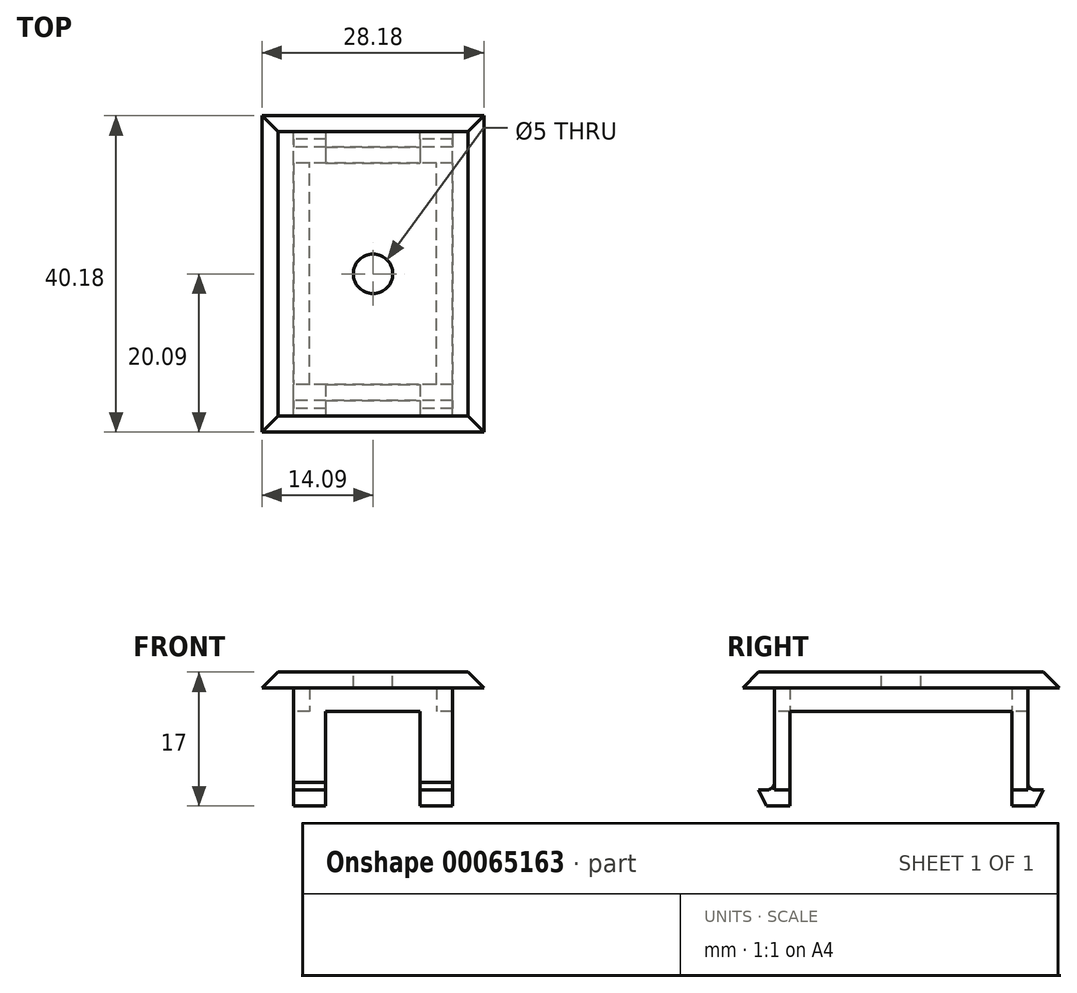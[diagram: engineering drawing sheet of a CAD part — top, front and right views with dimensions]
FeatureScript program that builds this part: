
annotation { "Feature Type Name" : "Feature", "Feature Type Description" : "" }
export const myFeature = defineFeature(function(context is Context, id is Id, definition is map)
    precondition{}
    {
        {
            var Q0;
            Q0=qCreatedBy(makeId("Top.planeOp"),FACE);
            var sketch = newSketch(context, id + "F0", { "sketchPlane" : qUnion([Q0])});
            skLineSegment(sketch, "E0.rect.bottom", {"start": v(10.1, -16.09) * mm, "end": v(-10.1, -16.09) * mm});
            skLineSegment(sketch, "E0.rect.top", {"start": v(10.1, 16.09) * mm, "end": v(-10.1, 16.09) * mm});
            skLineSegment(sketch, "E0.rect.left", {"start": v(10.1, -16.09) * mm, "end": v(10.1, 16.09) * mm});
            skLineSegment(sketch, "E0.rect.right", {"start": v(-10.1, -16.09) * mm, "end": v(-10.09, 16.09) * mm});
            skPoint(sketch, "E0.rect.middle", {"position": v(0, 0) * mm});
            skLineSegment(sketch, "E1.rect.bottom", {"start": v(8.1, 14.1) * mm, "end": v(-8.09, 14.1) * mm});
            skLineSegment(sketch, "E1.rect.top", {"start": v(8.09, -14.1) * mm, "end": v(-8.1, -14.1) * mm});
            skLineSegment(sketch, "E1.rect.left", {"start": v(8.1, 14.09) * mm, "end": v(8.1, -14.1) * mm});
            skLineSegment(sketch, "E1.rect.right", {"start": v(-8.1, 14.1) * mm, "end": v(-8.1, -14.09) * mm});
            skSolve(sketch);
        }
        {
            var Q0;
            Q0=makeQuery(id+"F0.imprint","IMPRINT",FACE,{"disambiguationData":[TD([[makeQuery(id+"F0.imprint","IMPRINT",EDGE,{"derivedFrom":sQuery(id+"F0.wireOp",EDGE,"E0.rect.bottom")}),-1.0]])]});
            extrude(context, id + "F1", {"entities" : qUnion([Q0]), "depth" : 13 * mm});
        }
        {
            var Q0;
            Q0=makeQuery(id+"F1.opExtrude","CAP_FACE",FACE,{"disambiguationData":[OSD([sQuery(id+"F0.wireOp",EDGE,"E0.rect.bottom"),sQuery(id+"F0.wireOp",EDGE,"E0.rect.top"),sQuery(id+"F0.wireOp",EDGE,"E0.rect.left"),sQuery(id+"F0.wireOp",EDGE,"E0.rect.right"),sQuery(id+"F0.wireOp",EDGE,"E1.rect.bottom"),sQuery(id+"F0.wireOp",EDGE,"E1.rect.top"),sQuery(id+"F0.wireOp",EDGE,"E1.rect.left"),sQuery(id+"F0.wireOp",EDGE,"E1.rect.right")])],"isStart":false});
            var sketch = newSketch(context, id + "F2", { "sketchPlane" : qUnion([Q0])});
            skLineSegment(sketch, "E2.rect.bottom", {"start": v(14.1, 20.09) * mm, "end": v(-14.09, 20.09) * mm});
            skLineSegment(sketch, "E2.rect.top", {"start": v(14.1, -20.09) * mm, "end": v(-14.09, -20.09) * mm});
            skLineSegment(sketch, "E2.rect.left", {"start": v(14.1, 20.09) * mm, "end": v(14.1, -20.09) * mm});
            skLineSegment(sketch, "E2.rect.right", {"start": v(-14.09, 20.09) * mm, "end": v(-14.09, -20.09) * mm});
            skPoint(sketch, "E2.rect.middle", {"position": v(0, 0) * mm});
            skSolve(sketch);
        }
        {
            var Q0;
            Q0=makeQuery(id+"F2.imprint","IMPRINT",FACE,{"disambiguationData":[TD([[makeQuery(id+"F2.imprint","IMPRINT",EDGE,{"derivedFrom":makeQuery(id+"F1.opExtrude","CAP_EDGE",EDGE,{"disambiguationData":[OSD([sQuery(id+"F0.wireOp",EDGE,"E1.rect.bottom")])],"isStart":false})}),1.0]])]});
            var Q1;
            Q1=makeQuery(id+"F2.imprint","IMPRINT",FACE,{"disambiguationData":[TD([[makeQuery(id+"F2.imprint","IMPRINT",EDGE,{"derivedFrom":makeQuery(id+"F1.opExtrude","CAP_EDGE",EDGE,{"disambiguationData":[OSD([sQuery(id+"F0.wireOp",EDGE,"E0.rect.bottom")])],"isStart":false})}),-1.0]])]});
            var Q2;
            Q2=makeQuery(id+"F2.imprint","IMPRINT",FACE,{"disambiguationData":[TD([[makeQuery(id+"F2.imprint","IMPRINT",EDGE,{"derivedFrom":sQuery(id+"F2.wireOp",EDGE,"E2.rect.bottom")}),1.0]])]});
            extrude(context, id + "F3", {"entities" : qUnion([Q0, Q1, Q2]), "operationType" : NewBodyOperationType.ADD, "depth" : 2 * mm});
        }
        {
            var Q0;
            Q0=makeQuery(id+"F3.opExtrude","CAP_EDGE",EDGE,{"disambiguationData":[OSD([sQuery(id+"F2.wireOp",EDGE,"E2.rect.top")])],"isStart":false});
            var Q1;
            Q1=makeQuery(id+"F3.opExtrude","CAP_EDGE",EDGE,{"disambiguationData":[OSD([sQuery(id+"F2.wireOp",EDGE,"E2.rect.right")])],"isStart":false});
            var Q2;
            Q2=makeQuery(id+"F3.opExtrude","CAP_EDGE",EDGE,{"disambiguationData":[OSD([sQuery(id+"F2.wireOp",EDGE,"E2.rect.bottom")])],"isStart":false});
            var Q3;
            Q3=makeQuery(id+"F3.opExtrude","CAP_EDGE",EDGE,{"disambiguationData":[OSD([sQuery(id+"F2.wireOp",EDGE,"E2.rect.left")])],"isStart":false});
            chamfer(context, id + "F4", {"entities" : qUnion([Q0, Q1, Q2, Q3]), "width" : 2 * mm, "tangentPropagation" : true});
        }
        {
            var Q0;
            Q0=makeQuery(id+"F3.opExtrude","CAP_FACE",FACE,{"disambiguationData":[OSD([sQuery(id+"F2.wireOp",EDGE,"E2.rect.bottom"),sQuery(id+"F2.wireOp",EDGE,"E2.rect.top"),sQuery(id+"F2.wireOp",EDGE,"E2.rect.left"),sQuery(id+"F2.wireOp",EDGE,"E2.rect.right")])],"isStart":false});
            var sketch = newSketch(context, id + "F5", { "sketchPlane" : qUnion([Q0])});
            skPoint(sketch, "E3", {"position": v(0, 0) * mm});
            skSolve(sketch);
        }
        {
            var Q0;
            Q0=sQuery(id+"F5.wireOp",VERTEX,"E3");
            var Q1;
            Q1=makeQuery(id+"F1.opExtrude","SWEPT_BODY",BODY,{"disambiguationData":[OSD([sQuery(id+"F0.wireOp",EDGE,"E0.rect.bottom"),sQuery(id+"F0.wireOp",EDGE,"E0.rect.top"),sQuery(id+"F0.wireOp",EDGE,"E0.rect.left"),sQuery(id+"F0.wireOp",EDGE,"E0.rect.right"),sQuery(id+"F0.wireOp",EDGE,"E1.rect.bottom"),sQuery(id+"F0.wireOp",EDGE,"E1.rect.top"),sQuery(id+"F0.wireOp",EDGE,"E1.rect.left"),sQuery(id+"F0.wireOp",EDGE,"E1.rect.right")])]});
            hole(context, id + "F6", {"style" : HoleStyle.SIMPLE, "holeDiameter" : 5 * mm, "endStyle" : HoleEndStyle.THROUGH, "locations" : qUnion([Q0]), "scope" : qUnion([Q1])});
        }
        {
            var Q0;
            Q0=makeQuery(id+"F1.opExtrude","SWEPT_FACE",FACE,{"disambiguationData":[OSD([sQuery(id+"F0.wireOp",EDGE,"E0.rect.right")])]});
            var sketch = newSketch(context, id + "F7", { "sketchPlane" : qUnion([Q0])});
            skLineSegment(sketch, "E4.rect.bottom", {"start": v(18.1, 0) * mm, "end": v(17.09, 0) * mm});
            skLineSegment(sketch, "E4.rect.top", {"start": v(17.09, -2) * mm, "end": v(-17.09, -2) * mm});
            skPoint(sketch, "E4.rect.middle", {"position": v(0, -1.06) * mm});
            skLineSegment(sketch, "E5", {"start": v(-18.1, 0) * mm, "end": v(-17.09, -2) * mm});
            skLineSegment(sketch, "E6", {"start": v(18.1, 0) * mm, "end": v(17.09, -2) * mm});
            skLineSegment(sketch, "E7", {"start": v(-16.09, 0) * mm, "end": v(-16.09, 6.93) * mm});
            skLineSegment(sketch, "E8", {"start": v(16.09, 0) * mm, "end": v(16.09, 6.05) * mm});
            skArc(sketch, "E9", {"start": v(-17.09, 0) * mm, "mid": v(-16.38, 0.3) * mm, "end": v(-16.09, 1) * mm});
            skArc(sketch, "E10", {"start": v(16.09, 1) * mm, "mid": v(16.38, 0.3) * mm, "end": v(17.09, 0) * mm});
            skLineSegment(sketch, "E11.trimOffspring", {"start": v(16.09, 0) * mm, "end": v(-16.09, 0) * mm});
            skLineSegment(sketch, "E12.trimOffspring", {"start": v(-17.09, 0) * mm, "end": v(-18.1, 0) * mm});
            skSolve(sketch);
        }
        {
            var Q0;
            Q0 = qSketchRegion(id + "F7", true);
            extrude(context, id + "F8", {"entities" : qUnion([Q0]), "oppositeDirection" : true, "depth" : 20.18 * mm});
        }
        {
            var Q0;
            Q0=makeQuery(id+"F1.opExtrude","SWEPT_FACE",FACE,{"disambiguationData":[OSD([sQuery(id+"F0.wireOp",EDGE,"E0.rect.right")])]});
            var sketch = newSketch(context, id + "F9", { "sketchPlane" : qUnion([Q0])});
            skLineSegment(sketch, "E13.rect.top", {"start": v(14.1, -2) * mm, "end": v(-14.1, -2) * mm});
            skLineSegment(sketch, "E13.rect.left", {"start": v(14.1, 10) * mm, "end": v(14.1, -2) * mm});
            skLineSegment(sketch, "E13.rect.right", {"start": v(-14.1, 10) * mm, "end": v(-14.1, -2) * mm});
            skLineSegment(sketch, "E14", {"start": v(-14.1, 10) * mm, "end": v(14.09, 10) * mm});
            skSolve(sketch);
        }
        {
            var Q0;
            Q0 = qSketchRegion(id + "F9", true);
            extrude(context, id + "F10", {"entities" : qUnion([Q0]), "operationType" : NewBodyOperationType.REMOVE, "oppositeDirection" : true, "depth" : 25 * mm});
        }
        {
            var Q0;
            Q0=qCreatedBy(makeId("Front.planeOp"),FACE);
            var sketch = newSketch(context, id + "F11", { "sketchPlane" : qUnion([Q0])});
            skLineSegment(sketch, "E15.rect.bottom", {"start": v(-6, 10) * mm, "end": v(6, 10) * mm});
            skLineSegment(sketch, "E15.rect.top", {"start": v(-6, -10) * mm, "end": v(6, -10) * mm});
            skLineSegment(sketch, "E15.rect.left", {"start": v(-6, 10) * mm, "end": v(-6, -10) * mm});
            skLineSegment(sketch, "E15.rect.right", {"start": v(6, 10) * mm, "end": v(6, -10) * mm});
            skPoint(sketch, "E15.rect.middle", {"position": v(0, 0) * mm});
            skSolve(sketch);
        }
        {
            var Q0;
            Q0=makeQuery(id+"F11.imprint","IMPRINT",FACE,{"disambiguationData":[TD([[makeQuery(id+"F11.imprint","IMPRINT",EDGE,{"derivedFrom":sQuery(id+"F11.wireOp",EDGE,"E15.rect.bottom")}),-1.0]])]});
            extrude(context, id + "F12", {"entities" : qUnion([Q0]), "operationType" : NewBodyOperationType.REMOVE, "endBound" : BoundingType.SYMMETRIC, "oppositeDirection" : true, "depth" : 50 * mm});
        }
    });
